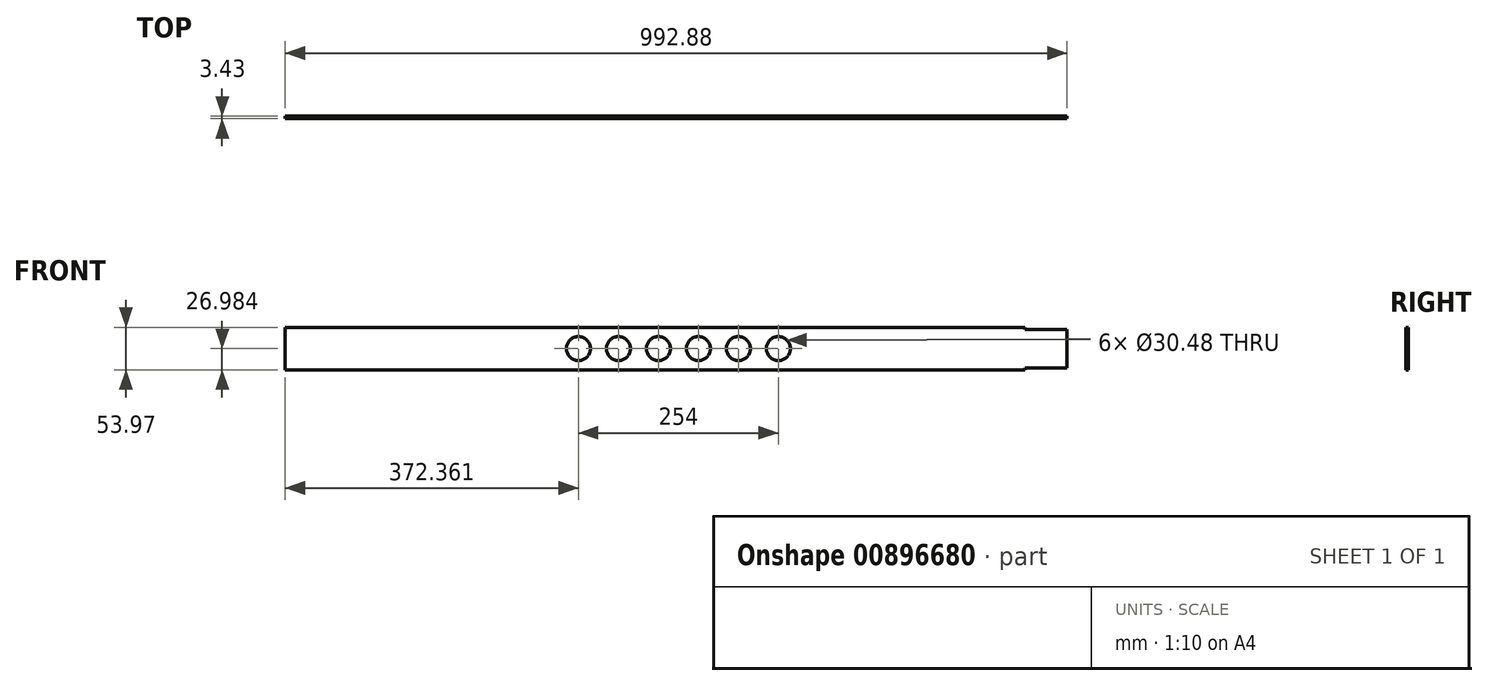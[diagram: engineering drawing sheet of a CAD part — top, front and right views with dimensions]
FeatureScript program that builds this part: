
annotation { "Feature Type Name" : "Feature", "Feature Type Description" : "" }
export const myFeature = defineFeature(function(context is Context, id is Id, definition is map)
    precondition{}
    {
        {
            var Q0;
            Q0=qCreatedBy(makeId("Front.planeOp"),FACE);
            var sketch = newSketch(context, id + "F0", { "sketchPlane" : qUnion([Q0])});
            skCircle(sketch, "E0", {"center": v(269.84, 554.38) * mm, "radius": 15.24 * mm});
            skCircle(sketch, "E1", {"center": v(371.44, 554.38) * mm, "radius": 15.24 * mm});
            skCircle(sketch, "E2", {"center": v(473.04, 554.38) * mm, "radius": 15.24 * mm});
            skLineSegment(sketch, "E3", {"start": v(837.28, 578.83) * mm, "end": v(837.28, 581.37) * mm});
            skLineSegment(sketch, "E4", {"start": v(890.36, 578.83) * mm, "end": v(837.28, 578.83) * mm});
            skLineSegment(sketch, "E5", {"start": v(890.36, 529.94) * mm, "end": v(890.36, 578.83) * mm});
            skLineSegment(sketch, "E6", {"start": v(837.28, 529.94) * mm, "end": v(890.36, 529.94) * mm});
            skLineSegment(sketch, "E7", {"start": v(837.28, 527.4) * mm, "end": v(837.28, 529.94) * mm});
            skLineSegment(sketch, "E8", {"start": v(-102.52, 527.4) * mm, "end": v(837.28, 527.4) * mm});
            skLineSegment(sketch, "E9", {"start": v(-102.52, 581.37) * mm, "end": v(-102.52, 527.4) * mm});
            skLineSegment(sketch, "E10", {"start": v(837.28, 581.37) * mm, "end": v(-102.52, 581.37) * mm});
            skCircle(sketch, "E11", {"center": v(523.84, 554.38) * mm, "radius": 15.24 * mm});
            skCircle(sketch, "E12", {"center": v(422.24, 554.38) * mm, "radius": 15.24 * mm});
            skCircle(sketch, "E13", {"center": v(320.64, 554.38) * mm, "radius": 15.24 * mm});
            skSolve(sketch);
        }
        {
            var Q0;
            Q0 = qSketchRegion(id + "F0", true);
            extrude(context, id + "F1", {"entities" : qUnion([Q0]), "depth" : 3.43 * mm, "offsetDistance" : 25.4 * mm});
        }
    });
